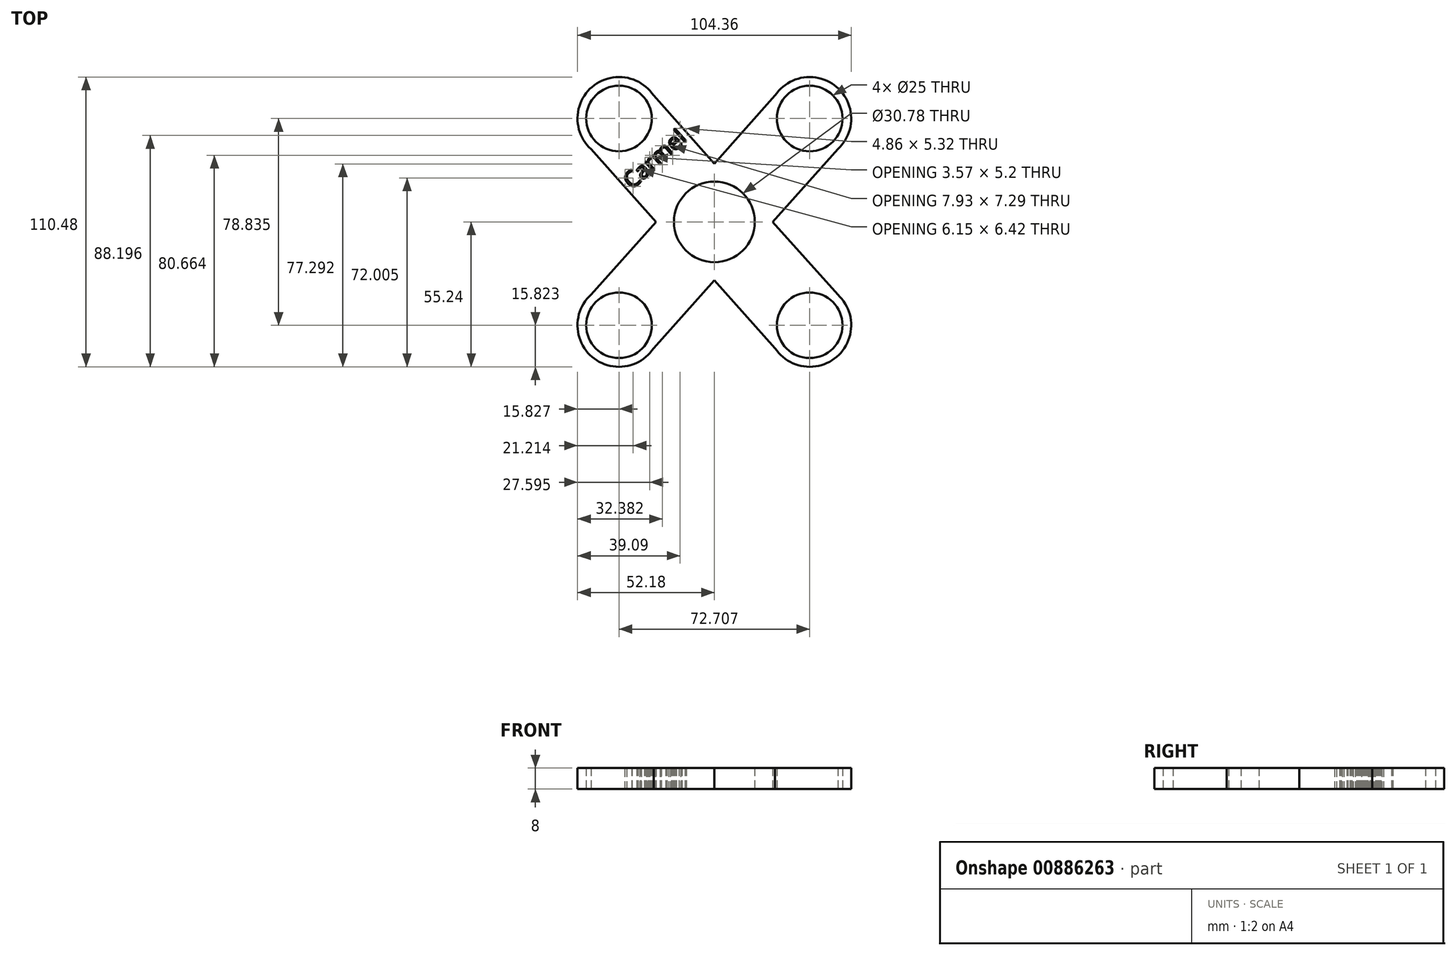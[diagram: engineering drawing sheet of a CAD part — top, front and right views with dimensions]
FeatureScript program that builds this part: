
annotation { "Feature Type Name" : "Feature", "Feature Type Description" : "" }
export const myFeature = defineFeature(function(context is Context, id is Id, definition is map)
    precondition{}
    {
        {
            var Q0;
            Q0=qCreatedBy(makeId("Top.planeOp"),FACE);
            var sketch = newSketch(context, id + "F0", { "sketchPlane" : qUnion([Q0])});
            skCircle(sketch, "E0", {"center": v(0, 0) * mm, "radius": 22.24 * mm});
            skLineSegment(sketch, "E1", {"start": v(0, 22.24) * mm, "end": v(-23.16, 48.16) * mm});
            skLineSegment(sketch, "E2", {"start": v(-22.24, 0) * mm, "end": v(-47.05, 27.76) * mm});
            skArc(sketch, "E3", {"start": v(-23.16, 48.16) * mm, "mid": v(-46.63, 51.45) * mm, "end": v(-47.05, 27.76) * mm});
            skPoint(sketch, "E3.third.point", {"position": v(-47.05, 51.08) * mm});
            skLineSegment(sketch, "E4.MirrorCS", {"start": v(0, 22.24) * mm, "end": v(23.16, 48.16) * mm});
            skLineSegment(sketch, "E5.MirrorCS", {"start": v(22.24, 0) * mm, "end": v(47.05, 27.76) * mm});
            skArc(sketch, "E6.MirrorCS", {"start": v(23.16, 48.16) * mm, "mid": v(46.63, 51.45) * mm, "end": v(47.05, 27.76) * mm});
            skLineSegment(sketch, "E7.MirrorCS", {"start": v(-22.24, 0) * mm, "end": v(-47.05, -27.76) * mm});
            skLineSegment(sketch, "E8.MirrorCS", {"start": v(0, -22.24) * mm, "end": v(-23.16, -48.16) * mm});
            skArc(sketch, "E9.MirrorCS", {"start": v(-23.16, -48.16) * mm, "mid": v(-46.63, -51.45) * mm, "end": v(-47.05, -27.76) * mm});
            skLineSegment(sketch, "E10.MirrorCS", {"start": v(22.24, 0) * mm, "end": v(47.05, -27.76) * mm});
            skLineSegment(sketch, "E11.MirrorCS", {"start": v(0, -22.24) * mm, "end": v(23.16, -48.16) * mm});
            skArc(sketch, "E12.MirrorCS", {"start": v(23.16, -48.16) * mm, "mid": v(46.63, -51.45) * mm, "end": v(47.05, -27.76) * mm});
            skCircle(sketch, "E13", {"center": v(-36.35, 39.42) * mm, "radius": 12.5 * mm});
            skCircle(sketch, "E14", {"center": v(-36.35, -39.42) * mm, "radius": 12.5 * mm});
            skCircle(sketch, "E15", {"center": v(36.35, -39.42) * mm, "radius": 12.5 * mm});
            skCircle(sketch, "E16", {"center": v(36.35, 39.42) * mm, "radius": 12.5 * mm});
            skCircle(sketch, "E17", {"center": v(0, 0) * mm, "radius": 15.4 * mm});
            skSolve(sketch);
        }
        {
            var Q0;
            Q0 = qSketchRegion(id + "F0", true);
            extrude(context, id + "F1", {"entities" : qUnion([Q0]), "depth" : 8 * mm, "offsetDistance" : 25 * mm});
        }
        {
            var Q0;
            Q0=qCreatedBy(makeId("Top.planeOp"),FACE);
            var sketch = newSketch(context, id + "F2", { "sketchPlane" : qUnion([Q0])});
            skText(sketch, "E18", { "text": "Carmel", "fontName": "OpenSans-Regular.ttf"});
            const initialGuessF2  = {"E18": [-0.03145, 0.01218, 0.7456, 0.6664, 0.00617]};
            skSetInitialGuess(sketch, initialGuessF2);
            skSolve(sketch);
        }
        {
            var Q0;
            Q0 = qSketchRegion(id + "F2", true);
            extrude(context, id + "F3", {"entities" : qUnion([Q0]), "operationType" : NewBodyOperationType.REMOVE, "depth" : 11.5 * mm, "offsetDistance" : 25 * mm});
        }
    });
